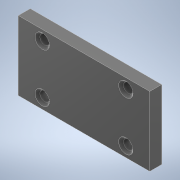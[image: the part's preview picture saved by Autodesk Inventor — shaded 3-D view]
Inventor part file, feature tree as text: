
AUTODESK INVENTOR PART (.ipt)
format: ipt  version: 2021 (Build 250183000, 183)  size: 115,200 bytes
history: native  units: mm
features: sketch x2, other x1, extrude x1, hole x1
ambient origin geometry x8: Origin, YZ Plane, XZ Plane, XY Plane, X Axis, Y Axis, Z Axis, Center Point
bodies: Body1 (feature_tree)
feature tree (5):
  other  "Sólido1"
  extrude  "Extrusão1"  Depth=29.0mm
  hole  "Furo1"  [1 undecoded]
  sketch  "Esboço1"  dims[d0=55.0mm d1=29.0mm]
  sketch  "Esboço2"  dims[d2=5.0mm d3=0.0mm d4=10.0mm d5=4.25mm d6=4.0mm d7=6.0mm d8=6.0mm d9=2.0mm d10=90.0deg d11=8.0mm d12=20.594885mm]
note: 1 required parameter value undecoded (feature->parameter linkage not recoverable at this tier; creation-order binding heuristic only, values carry confidence <= 0.55)
